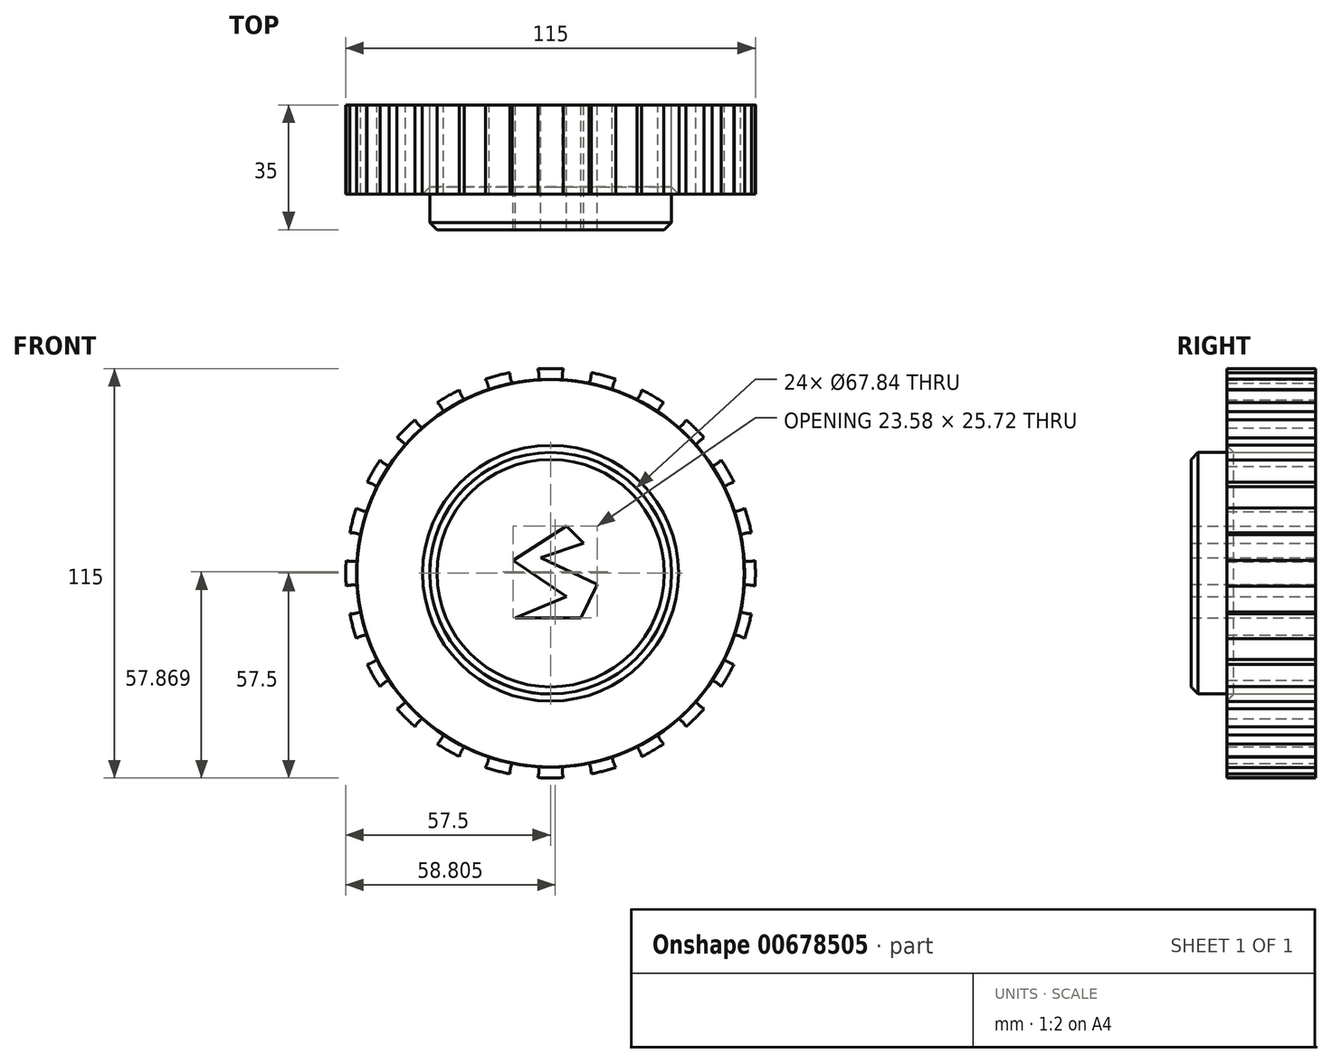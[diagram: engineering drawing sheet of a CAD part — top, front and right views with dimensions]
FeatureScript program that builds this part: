
annotation { "Feature Type Name" : "Feature", "Feature Type Description" : "" }
export const myFeature = defineFeature(function(context is Context, id is Id, definition is map)
    precondition{}
    {
        {
            var Q0;
            Q0=qCreatedBy(makeId("Front.planeOp"),FACE);
            var sketch = newSketch(context, id + "F0", { "sketchPlane" : qUnion([Q0])});
            skArc(sketch, "E0", {"start": v(0, 53.72) * mm, "mid": v(-1.76, 53.7) * mm, "end": v(-3.51, 53.6) * mm, "construction": true});
            skCircle(sketch, "E1", {"center": v(0, 0) * mm, "radius": 58.67 * mm, "construction": true});
            skCircle(sketch, "E2", {"center": v(0, 0) * mm, "radius": 63.5 * mm, "construction": true});
            skLineSegment(sketch, "E3", {"start": v(0, 0) * mm, "end": v(0, 76.02) * mm, "construction": true});
            skLineSegment(sketch, "E4", {"start": v(0, 0) * mm, "end": v(-5.05, 77.08) * mm, "construction": true});
            skLineSegment(sketch, "E5", {"start": v(-15.1, 55.49) * mm, "end": v(-17.93, 54.72) * mm, "construction": true});
            skArc(sketch, "E6", {"start": v(-17.91, 54.64) * mm, "mid": v(16.5, -55.08) * mm, "end": v(-15.1, 55.49) * mm, "construction": true});
            skArc(sketch, "E7", {"start": v(0, 35.45) * mm, "mid": v(-1.16, 35.44) * mm, "end": v(-2.32, 35.38) * mm});
            skArc(sketch, "E8", {"start": v(57.5, 0) * mm, "mid": v(34.92, 45.69) * mm, "end": v(-15.1, 55.49) * mm});
            skCircle(sketch, "E9", {"center": v(0, 0) * mm, "radius": 54.44 * mm});
            skCircle(sketch, "E10", {"center": v(-3.84, 58.55) * mm, "radius": 14.6 * mm, "construction": true});
            skLineSegment(sketch, "E11", {"start": v(-0.04, 58.67) * mm, "end": v(-39.9, 63.87) * mm, "construction": true});
            skLineSegment(sketch, "E12", {"start": v(-0.04, 58.67) * mm, "end": v(-37.32, 50.35) * mm, "construction": true});
            skArc(sketch, "E13.trimOffspring", {"start": v(-3.57, 57.4) * mm, "mid": v(-3.77, 58.3) * mm, "end": v(-4.03, 59.2) * mm, "construction": true});
            skArc(sketch, "E14.trimOffspring", {"start": v(-3.46, 52.76) * mm, "mid": v(-3.37, 53.54) * mm, "end": v(-3.33, 54.34) * mm, "construction": true});
            skArc(sketch, "E15.trimOffspring", {"start": v(-31.56, 49.46) * mm, "mid": v(-31.33, 48.91) * mm, "end": v(-31.09, 48.38) * mm, "construction": true});
            skCircle(sketch, "E16", {"center": v(-17.91, 54.64) * mm, "radius": 14.6 * mm, "construction": true});
            skArc(sketch, "E17", {"start": v(-3.57, 57.4) * mm, "mid": v(-4.43, 60.47) * mm, "end": v(-6.08, 63.2) * mm});
            skArc(sketch, "E18", {"start": v(-3.51, 53.6) * mm, "mid": v(-3.29, 55.5) * mm, "end": v(-3.57, 57.4) * mm});
            skPoint(sketch, "E19.orphan", {"position": v(6.08, 63.2) * mm});
            skPoint(sketch, "E20.MirrorCS.start.orphan", {"position": v(3.57, 57.4) * mm});
            skPoint(sketch, "E21.MirrorCS.start.orphan", {"position": v(3.51, 53.6) * mm});
            skArc(sketch, "E22.MirrorCS", {"start": v(3.51, 53.6) * mm, "mid": v(3.29, 55.5) * mm, "end": v(3.57, 57.4) * mm});
            skCircle(sketch, "E23", {"center": v(0, 0) * mm, "radius": 33.92 * mm});
            skCircle(sketch, "E24", {"center": v(0, 0) * mm, "radius": 21.7 * mm});
            skLineSegment(sketch, "E25", {"start": v(0, 15.72) * mm, "end": v(-1.03, 15.72) * mm});
            skPoint(sketch, "E26.start.orphan", {"position": v(-18.8, 0) * mm});
            skPoint(sketch, "E27.start.orphan", {"position": v(18.05, 0) * mm});
            skPoint(sketch, "E28.end.orphan", {"position": v(-4.96, 21.13) * mm});
            skPoint(sketch, "E29.orphan", {"position": v(-4.96, 15.72) * mm});
            skLineSegment(sketch, "E30", {"start": v(4.52, 13.23) * mm, "end": v(-10.48, 3.58) * mm});
            skLineSegment(sketch, "E31", {"start": v(-10.48, 3.58) * mm, "end": v(4.52, -6.6) * mm});
            skLineSegment(sketch, "E32", {"start": v(4.52, -6.6) * mm, "end": v(-9.95, -12.5) * mm});
            skLineSegment(sketch, "E33", {"start": v(-9.95, -12.5) * mm, "end": v(8.54, -12.5) * mm});
            skLineSegment(sketch, "E34", {"start": v(8.54, -12.5) * mm, "end": v(13.1, -3.11) * mm});
            skLineSegment(sketch, "E35", {"start": v(13.1, -3.11) * mm, "end": v(-2.71, 4.39) * mm});
            skLineSegment(sketch, "E36", {"start": v(-2.71, 4.39) * mm, "end": v(9.34, 8.4) * mm});
            skLineSegment(sketch, "E37", {"start": v(9.34, 8.4) * mm, "end": v(4.52, 13.23) * mm});
            skSolve(sketch);
        }
        {
            var Q0;
            Q0 = qSketchRegion(id + "F0", true);
            extrude(context, id + "F1", {"entities" : qUnion([Q0]), "depth" : 25 * mm, "offsetDistance" : 25 * mm});
        }
        {
            var Q0;
            Q0=makeQuery(id+"F1.opExtrude","SWEPT_BODY",BODY,{"disambiguationData":[OSD([sQuery(id+"F0.wireOp",EDGE,"E8"),sQuery(id+"F0.wireOp",EDGE,"E9"),sQuery(id+"F0.wireOp",EDGE,"E18"),sQuery(id+"F0.wireOp",EDGE,"E22.MirrorCS")])]});
            var Q1;
            Q1=sQuery(id+"F0.wireOp",EDGE,"E9");
            circularPattern(context, id + "F2", {"entities" : qUnion([Q0]), "axis" : qUnion([Q1]), "angle" : 360 * degree, "instanceCount" : 24, "equalSpace" : true});
        }
        {
            var Q0;
            Q0=makeQuery(id+"F0.imprint","IMPRINT",FACE,{"disambiguationData":[TD([[makeQuery(id+"F0.imprint","IMPRINT",EDGE,{"derivedFrom":sQuery(id+"F0.wireOp",EDGE,"E23")}),1.0]])]});
            var Q1;
            Q1=makeQuery(id+"F0.imprint","IMPRINT",FACE,{"disambiguationData":[TD([[makeQuery(id+"F0.imprint","IMPRINT",EDGE,{"derivedFrom":sQuery(id+"F0.wireOp",EDGE,"E24")}),1.0]])]});
            extrude(context, id + "F3", {"entities" : qUnion([Q0, Q1]), "depth" : 35 * mm, "offsetDistance" : 25 * mm});
        }
        {
            var Q0;
            Q0=makeQuery(id+"F3.opExtrude","CAP_EDGE",EDGE,{"disambiguationData":[OSD([sQuery(id+"F0.wireOp",EDGE,"E23")])],"isStart":false});
            var Q1;
            Q1=makeQuery(id+"F1.opExtrude","CAP_EDGE",EDGE,{"disambiguationData":[OSD([sQuery(id+"F0.wireOp",EDGE,"E23")])],"isStart":false});
            chamfer(context, id + "F4", {"entities" : qUnion([Q0, Q1]), "width" : 2 * mm, "tangentPropagation" : true});
        }
    });
